# Revit family: WC DRAKAR_RFA
name_source: partatom
category: Aparatos sanitarios
units: mm (PartAtom-declared; Revit-internal decimal feet)

## family parameters
Compartido = No
Corte con vacíos al cargar = No
Cota de conector redondo = Diámetro de uso
Número OmniClass = 23.45.00.00
Punto de cálculo de habitación = No
Se basa en plano de trabajo = No
Siempre vertical = Sí
Tipo de pieza = Normal
Título OmniClass = Sanitary, Laundry, and Cleaning Equipment

## types (1)
- WC DRAKAR
    Certification = https://helvex.com.mx
    Comentarios de tipo = SANIVEX
    Compliance = NOM-009-CONAGUA-2001
    Conexión AF = Sí
    Data Sheet = https://helvex.com.mx
    Descripción = Diseño ergonómico de construcción robusta con cerámica de 10mm de espesor, con sistema de descarga tipo vórtice con sifón jet y espejo de agua óptimo, mueble libre de alabeo (base plana).
    Elevación por defecto = 0"
    Fabricante = HELVEX
    High Gloss Ceramic = High Gloss Ceramic
    Inlet Threads = Feeding: Ø 15/16" - 14 NS-1 Flush: Coupled With Sanitary Flange
    Max. Working Pressure = 85.3 psi
    Maximum Consumption = 1.26 gpf
    Min. Working Pressure = 14.2 psi
    Modelo = WC DRAKAR
    Technical Details = Exposed Glazed Trapway; Siphon Action Jetted Bowl; Certified Intake And Flushing Valves; Silent Intake Valve; Flush Valve With Seal; Optimum Water Surface
    Total Height = 30"
    Total Length = 30"
    Total Width = 21"
    URL = https://helvex.com.mx
    Warranty = 5 Years Warranty In Iron Fittings

## geometry (parser evidence)
native form markers: Sweep x3
no freeform markers — native parametric forms only
